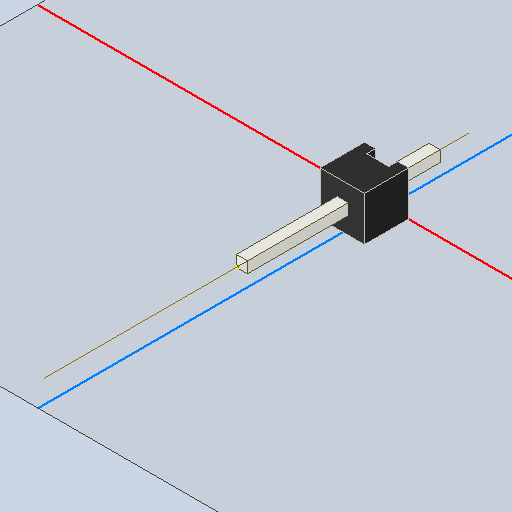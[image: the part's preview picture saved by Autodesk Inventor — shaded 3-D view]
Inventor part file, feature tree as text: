
AUTODESK INVENTOR PART (.ipt)
format: ipt  version: 2022 (Build 260153000, 153)  size: 117,760 bytes
history: native  units: mm
features: other x2, sketch x1
ambient origin geometry x8: Origin, YZ Plane, XZ Plane, XY Plane, X Axis, Y Axis, Z Axis, Center Point
bodies: Solid1 (feature_tree), Solid2 (feature_tree), Body (feature_tree)
feature tree (3):
  sketch  "Sketch1"
  other  "Work Axis2"
  other  "Pin"
